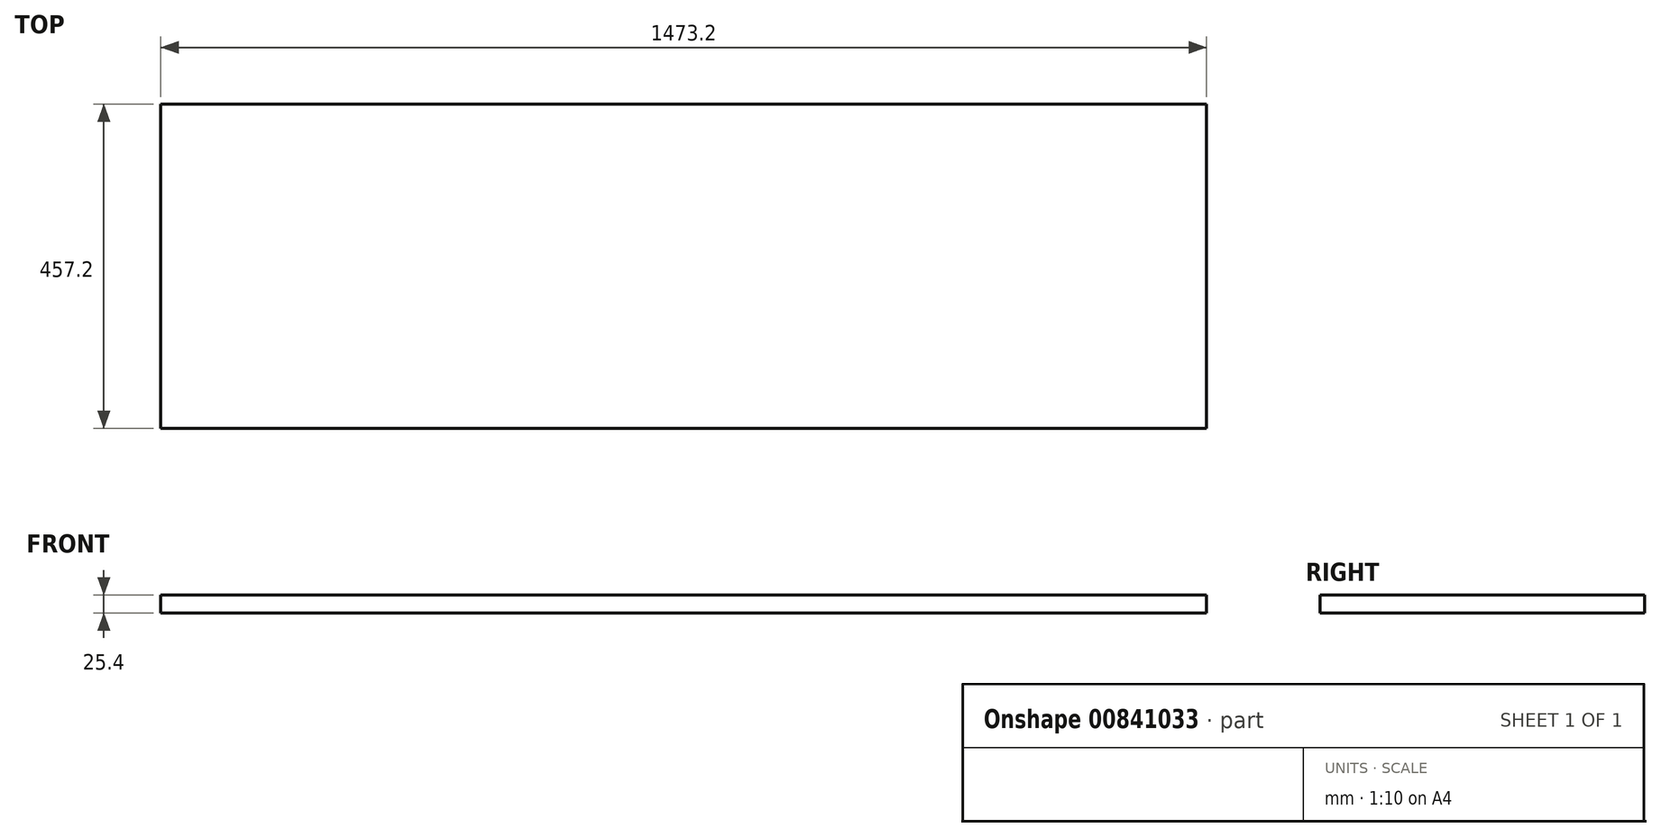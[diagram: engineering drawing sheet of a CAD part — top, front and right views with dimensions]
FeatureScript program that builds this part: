
annotation { "Feature Type Name" : "Feature", "Feature Type Description" : "" }
export const myFeature = defineFeature(function(context is Context, id is Id, definition is map)
    precondition{}
    {
        {
            var Q0;
            Q0=qCreatedBy(makeId("Top.planeOp"),FACE);
            var sketch = newSketch(context, id + "F0", { "sketchPlane" : qUnion([Q0])});
            skLineSegment(sketch, "E0.bottom", {"start": v(0, 0) * mm, "end": v(1473.2, 0) * mm});
            skLineSegment(sketch, "E0.top", {"start": v(0, 457.2) * mm, "end": v(1473.2, 457.2) * mm});
            skLineSegment(sketch, "E0.left", {"start": v(0, 0) * mm, "end": v(0, 457.2) * mm});
            skLineSegment(sketch, "E0.right", {"start": v(1473.2, 0) * mm, "end": v(1473.2, 457.2) * mm});
            skSolve(sketch);
        }
        {
            var Q0;
            Q0=makeQuery(id+"F0.imprint","IMPRINT",FACE,{"disambiguationData":[TD([[makeQuery(id+"F0.imprint","IMPRINT",EDGE,{"derivedFrom":sQuery(id+"F0.wireOp",EDGE,"E0.bottom")}),1.0]])]});
            extrude(context, id + "F1", {"entities" : qUnion([Q0]), "depth" : 25.4 * mm, "offsetDistance" : 25.4 * mm});
        }
    });
